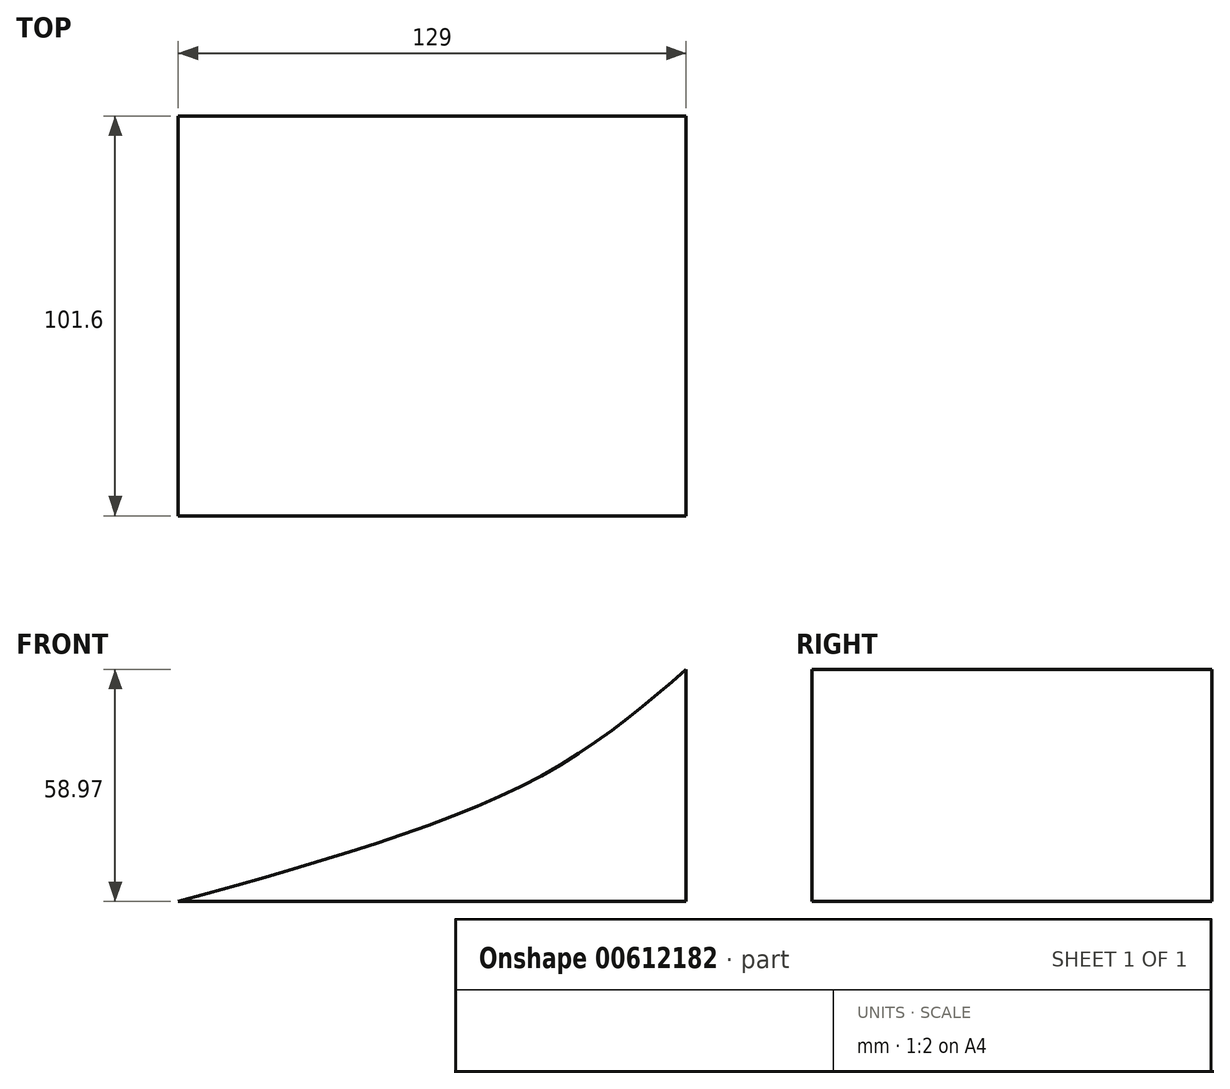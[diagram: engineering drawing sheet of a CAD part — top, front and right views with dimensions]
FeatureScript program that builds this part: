
annotation { "Feature Type Name" : "Feature", "Feature Type Description" : "" }
export const myFeature = defineFeature(function(context is Context, id is Id, definition is map)
    precondition{}
    {
        {
            var Q0;
            Q0=qCreatedBy(makeId("Front.planeOp"),FACE);
            var sketch = newSketch(context, id + "F0", { "sketchPlane" : qUnion([Q0])});
            skLineSegment(sketch, "E0", {"start": v(-65.73, 0) * mm, "end": v(63.27, 0) * mm});
            skLineSegment(sketch, "E1", {"start": v(63.27, 0) * mm, "end": v(63.27, 58.97) * mm});
            skFitSpline(sketch, "E2", {"points": [v(-65.73, 0) * mm, v(23.04, 30.1) * mm, v(63.27, 58.97) * mm], "startDerivative": vector(169.99, 47.16) * mm, "endDerivative": vector(83.45, 72.09) * mm});
            skSolve(sketch);
        }
        {
            var Q0;
            Q0=makeQuery(id+"F0.imprint","IMPRINT",FACE,{"disambiguationData":[TD([[makeQuery(id+"F0.imprint","IMPRINT",EDGE,{"derivedFrom":sQuery(id+"F0.wireOp",EDGE,"E0")}),1.0]])]});
            extrude(context, id + "F1", {"entities" : qUnion([Q0]), "depth" : 101.6 * mm, "offsetDistance" : 25.4 * mm});
        }
    });
